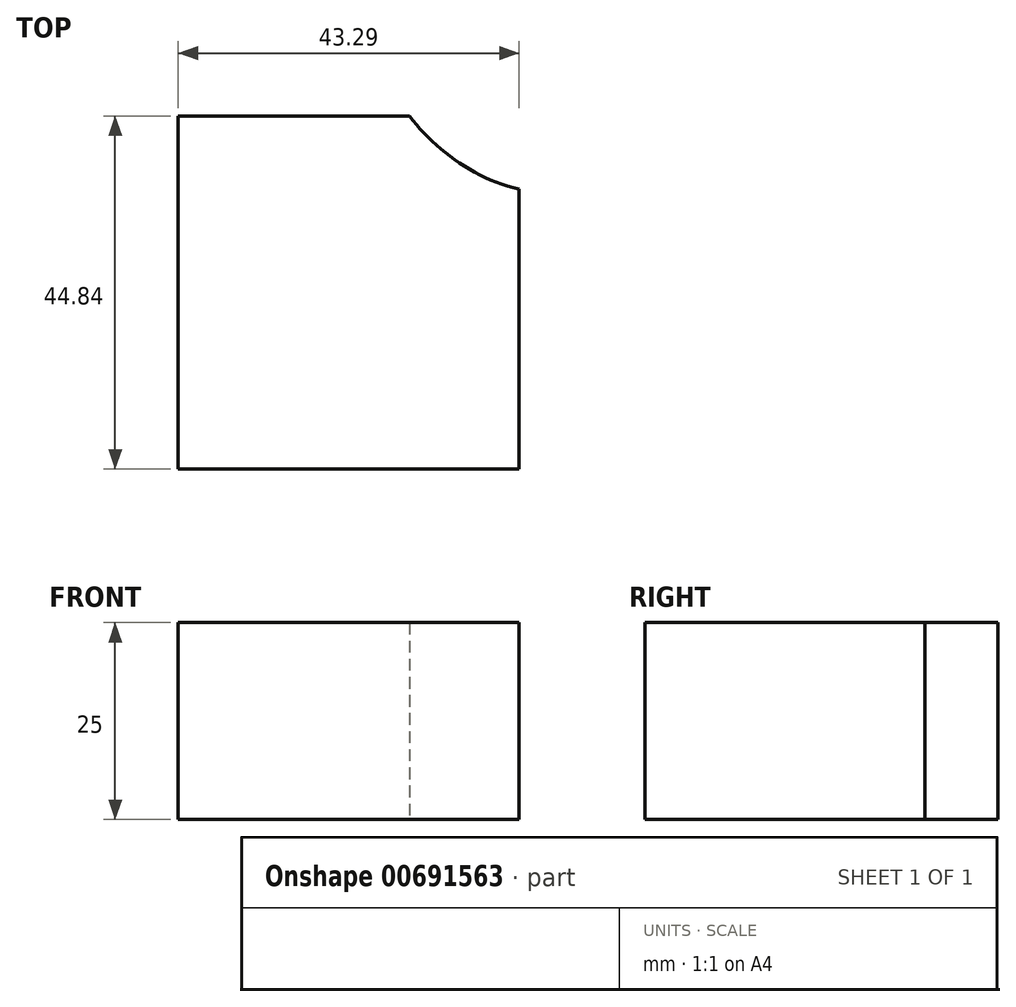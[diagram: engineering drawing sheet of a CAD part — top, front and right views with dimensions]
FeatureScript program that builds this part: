
annotation { "Feature Type Name" : "Feature", "Feature Type Description" : "" }
export const myFeature = defineFeature(function(context is Context, id is Id, definition is map)
    precondition{}
    {
        {
            var Q0;
            Q0=qCreatedBy(makeId("Top.planeOp"),FACE);
            var sketch = newSketch(context, id + "F0", { "sketchPlane" : qUnion([Q0])});
            skLineSegment(sketch, "E0.bottom", {"start": v(-90.25, 26.04) * mm, "end": v(-46.96, 26.04) * mm});
            skLineSegment(sketch, "E0.top", {"start": v(-90.25, -18.8) * mm, "end": v(-46.96, -18.8) * mm});
            skLineSegment(sketch, "E0.left", {"start": v(-90.25, 26.04) * mm, "end": v(-90.25, -18.8) * mm});
            skLineSegment(sketch, "E0.right", {"start": v(-46.96, 26.04) * mm, "end": v(-46.96, -18.8) * mm});
            skFitSpline(sketch, "E1", {"points": [v(-65.02, 36.32) * mm, v(-53.5, 45.35) * mm, v(-31.7, 34.45) * mm, v(-29.21, 44.73) * mm, v(-9.9, 47.22) * mm, v(-39.8, 16.39) * mm, v(-65.02, 36.32) * mm]});
            skSolve(sketch);
        }
        {
            var Q0;
            {var subQ1=sQuery(id+"F0.wireOp",EDGE,"E0.top");Q0=makeQuery(id+"F0.imprint","IMPRINT",FACE,{"disambiguationData":[TD([[makeQuery(id+"F0.imprint","IMPRINT",EDGE,{"derivedFrom":subQ1}),1.0]])]});}
            extrude(context, id + "F1", {"entities" : qUnion([Q0]), "depth" : 25 * mm, "offsetDistance" : 25 * mm});
        }
    });
